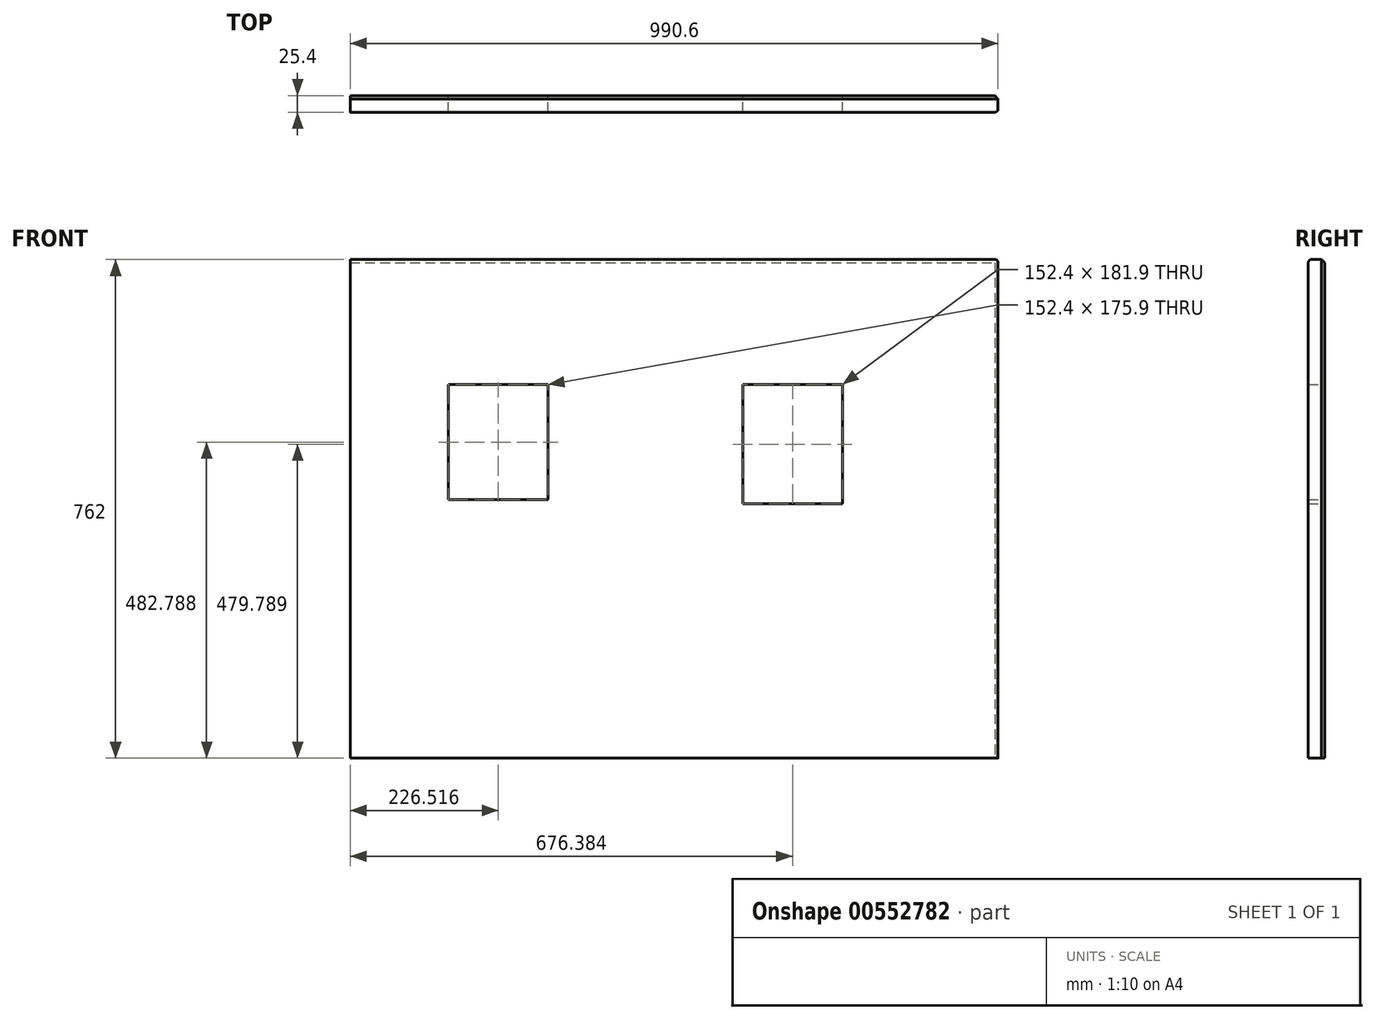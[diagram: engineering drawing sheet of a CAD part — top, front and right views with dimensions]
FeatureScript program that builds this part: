
annotation { "Feature Type Name" : "Feature", "Feature Type Description" : "" }
export const myFeature = defineFeature(function(context is Context, id is Id, definition is map)
    precondition{}
    {
        {
            var Q0;
            Q0=qCreatedBy(makeId("Front.planeOp"),FACE);
            var sketch = newSketch(context, id + "F0", { "sketchPlane" : qUnion([Q0])});
            skLineSegment(sketch, "E0.bottom", {"start": v(-494.4, 191.26) * mm, "end": v(496.2, 191.26) * mm});
            skLineSegment(sketch, "E0.top", {"start": v(-494.4, -570.74) * mm, "end": v(496.2, -570.74) * mm});
            skLineSegment(sketch, "E0.left", {"start": v(-494.4, 191.26) * mm, "end": v(-494.4, -570.74) * mm});
            skLineSegment(sketch, "E0.right", {"start": v(496.2, 191.26) * mm, "end": v(496.2, -570.74) * mm});
            skLineSegment(sketch, "E1.bottom", {"start": v(-344.1, 0) * mm, "end": v(-191.7, 0) * mm});
            skLineSegment(sketch, "E1.top", {"start": v(-344.1, -175.9) * mm, "end": v(-191.7, -175.9) * mm});
            skLineSegment(sketch, "E1.left", {"start": v(-344.1, 0) * mm, "end": v(-344.1, -175.9) * mm});
            skLineSegment(sketch, "E1.right", {"start": v(-191.7, 0) * mm, "end": v(-191.7, -175.9) * mm});
            skLineSegment(sketch, "E2.bottom", {"start": v(105.77, 0) * mm, "end": v(258.17, 0) * mm});
            skLineSegment(sketch, "E2.top", {"start": v(105.77, -181.9) * mm, "end": v(258.17, -181.9) * mm});
            skLineSegment(sketch, "E2.left", {"start": v(105.77, 0) * mm, "end": v(105.77, -181.9) * mm});
            skLineSegment(sketch, "E2.right", {"start": v(258.17, 0) * mm, "end": v(258.17, -181.9) * mm});
            skSolve(sketch);
        }
        {
            var Q0;
            Q0 = qSketchRegion(id + "F0", true);
            extrude(context, id + "F1", {"entities" : qUnion([Q0]), "depth" : 25.4 * mm, "offsetDistance" : 25.4 * mm});
        }
        {
            var Q0;
            Q0=makeQuery(id+"F1.opExtrude","CAP_EDGE",EDGE,{"disambiguationData":[OSD([sQuery(id+"F0.wireOp",EDGE,"E0.bottom")])],"isStart":false});
            fillet(context, id + "F2", {"entities" : qUnion([Q0]), "radius" : 5.08 * mm, "tangentPropagation" : true, "allowEdgeOverflow" : false});
        }
        {
            var Q0;
            {var subQ0=sQuery(id+"F0.wireOp",EDGE,"E0.bottom");Q0=makeQuery(id+"F2.opFillet","BLEND_EDGE",EDGE,{"blendedFrom":[makeQuery(id+"F1.opExtrude","CAP_EDGE",EDGE,{"disambiguationData":[OSD([subQ0])],"isStart":false}),makeQuery(id+"F1.opExtrude","CAP_FACE",FACE,{"disambiguationData":[OSD([subQ0,sQuery(id+"F0.wireOp",EDGE,"E0.top"),sQuery(id+"F0.wireOp",EDGE,"E0.left"),sQuery(id+"F0.wireOp",EDGE,"E0.right"),sQuery(id+"F0.wireOp",EDGE,"E1.bottom"),sQuery(id+"F0.wireOp",EDGE,"E1.top"),sQuery(id+"F0.wireOp",EDGE,"E1.left"),sQuery(id+"F0.wireOp",EDGE,"E1.right"),sQuery(id+"F0.wireOp",EDGE,"E2.bottom"),sQuery(id+"F0.wireOp",EDGE,"E2.top"),sQuery(id+"F0.wireOp",EDGE,"E2.left"),sQuery(id+"F0.wireOp",EDGE,"E2.right")])],"isStart":false})],"blendedInto":[makeQuery(id+"F1.opExtrude","CAP_FACE",FACE,{"disambiguationData":[OSD([subQ0,sQuery(id+"F0.wireOp",EDGE,"E0.top"),sQuery(id+"F0.wireOp",EDGE,"E0.left"),sQuery(id+"F0.wireOp",EDGE,"E0.right"),sQuery(id+"F0.wireOp",EDGE,"E1.bottom"),sQuery(id+"F0.wireOp",EDGE,"E1.top"),sQuery(id+"F0.wireOp",EDGE,"E1.left"),sQuery(id+"F0.wireOp",EDGE,"E1.right"),sQuery(id+"F0.wireOp",EDGE,"E2.bottom"),sQuery(id+"F0.wireOp",EDGE,"E2.top"),sQuery(id+"F0.wireOp",EDGE,"E2.left"),sQuery(id+"F0.wireOp",EDGE,"E2.right")])],"isStart":false})]});}
            var Q1;
            Q1=makeQuery(id+"F1.opExtrude","CAP_EDGE",EDGE,{"disambiguationData":[OSD([sQuery(id+"F0.wireOp",EDGE,"E0.right")])],"isStart":false});
            fillet(context, id + "F3", {"entities" : qUnion([Q0, Q1]), "radius" : 5.08 * mm, "tangentPropagation" : true, "allowEdgeOverflow" : false});
        }
        {
            var Q0;
            Q0=makeQuery(id+"F1.opExtrude","CAP_EDGE",EDGE,{"disambiguationData":[OSD([sQuery(id+"F0.wireOp",EDGE,"E0.right")])],"isStart":true});
            chamfer(context, id + "F4", {"entities" : qUnion([Q0]), "width" : 5.08 * mm, "tangentPropagation" : true});
        }
    });
